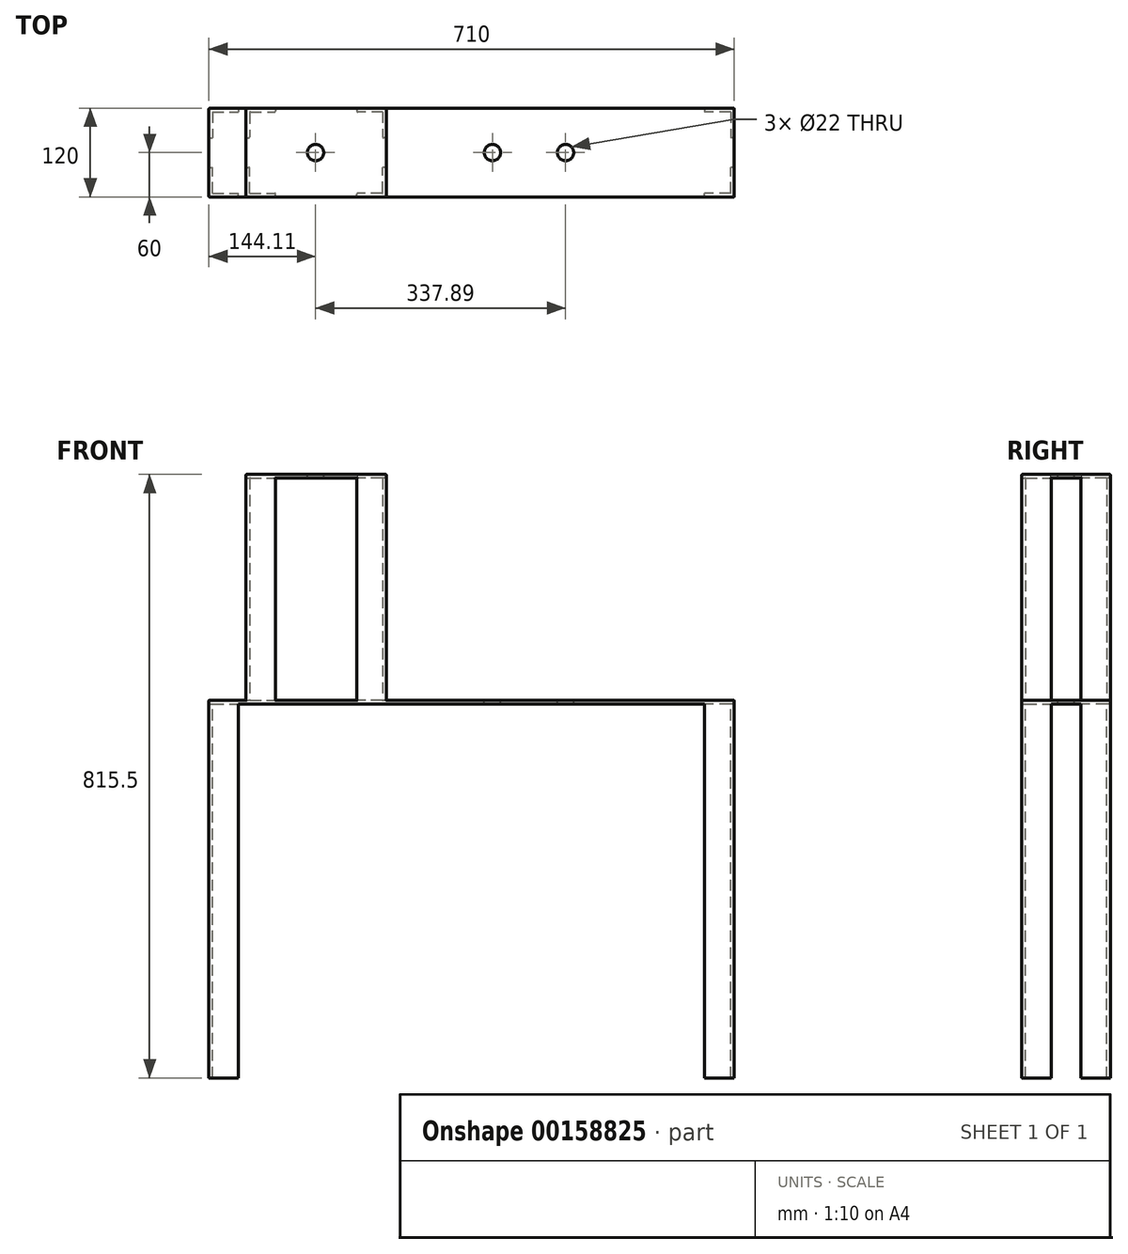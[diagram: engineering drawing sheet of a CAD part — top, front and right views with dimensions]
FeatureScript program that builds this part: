
annotation { "Feature Type Name" : "Feature", "Feature Type Description" : "" }
export const myFeature = defineFeature(function(context is Context, id is Id, definition is map)
    precondition{}
    {
        {
            var Q0;
            Q0=qCreatedBy(makeId("Top.planeOp"),FACE);
            var sketch = newSketch(context, id + "F0", { "sketchPlane" : qUnion([Q0])});
            skLineSegment(sketch, "E0.bottom", {"start": v(-355, -60) * mm, "end": v(355, -60) * mm});
            skLineSegment(sketch, "E0.top", {"start": v(-355, 60) * mm, "end": v(355, 60) * mm});
            skLineSegment(sketch, "E0.left", {"start": v(-355, -60) * mm, "end": v(-355, 60) * mm});
            skLineSegment(sketch, "E0.right", {"start": v(355, -60) * mm, "end": v(355, 60) * mm});
            skPoint(sketch, "E0.middle", {"position": v(0, 0) * mm});
            skSolve(sketch);
        }
        {
            var Q0;
            Q0=makeQuery(id+"F0.imprint","IMPRINT",FACE,{"disambiguationData":[TD([[makeQuery(id+"F0.imprint","IMPRINT",EDGE,{"derivedFrom":sQuery(id+"F0.wireOp",EDGE,"E0.bottom")}),1.0]])]});
            extrude(context, id + "F1", {"entities" : qUnion([Q0]), "depth" : 5 * mm});
        }
        {
            var Q0;
            Q0=makeQuery(id+"F1.opExtrude","CAP_FACE",FACE,{"disambiguationData":[OSD([sQuery(id+"F0.wireOp",EDGE,"E0.bottom"),sQuery(id+"F0.wireOp",EDGE,"E0.top"),sQuery(id+"F0.wireOp",EDGE,"E0.left"),sQuery(id+"F0.wireOp",EDGE,"E0.right")])],"isStart":true});
            var sketch = newSketch(context, id + "F2", { "sketchPlane" : qUnion([Q0])});
            skLineSegment(sketch, "E1", {"start": v(0, 84.03) * mm, "end": v(0, -87.79) * mm, "construction": true});
            skLineSegment(sketch, "E2", {"start": v(-372.84, 0) * mm, "end": v(344.3, 0) * mm, "construction": true});
            skSolve(sketch);
        }
        {
            var Q0;
            Q0=makeQuery(id+"F1.opExtrude","CAP_FACE",FACE,{"disambiguationData":[OSD([sQuery(id+"F0.wireOp",EDGE,"E0.bottom"),sQuery(id+"F0.wireOp",EDGE,"E0.top"),sQuery(id+"F0.wireOp",EDGE,"E0.left"),sQuery(id+"F0.wireOp",EDGE,"E0.right")])],"isStart":true});
            var sketch = newSketch(context, id + "F3", { "sketchPlane" : qUnion([Q0])});
            skLineSegment(sketch, "E3.bottom", {"start": v(-355, 60) * mm, "end": v(-350, 60) * mm});
            skLineSegment(sketch, "E3.top", {"start": v(-355, 20) * mm, "end": v(-350, 20) * mm});
            skLineSegment(sketch, "E3.left", {"start": v(-355, 60) * mm, "end": v(-355, 20) * mm});
            skLineSegment(sketch, "E3.right", {"start": v(-350, 55) * mm, "end": v(-350, 20) * mm});
            skLineSegment(sketch, "E4.bottom", {"start": v(-355, 60) * mm, "end": v(-315, 60) * mm});
            skLineSegment(sketch, "E4.top", {"start": v(-350, 55) * mm, "end": v(-315, 55) * mm});
            skLineSegment(sketch, "E4.left", {"start": v(-355, 60) * mm, "end": v(-355, 55) * mm});
            skLineSegment(sketch, "E4.right", {"start": v(-315, 60) * mm, "end": v(-315, 55) * mm});
            skLineSegment(sketch, "E5.MirrorCS", {"start": v(-350, -55) * mm, "end": v(-350, -20) * mm});
            skLineSegment(sketch, "E6.MirrorCS", {"start": v(-355, -60) * mm, "end": v(-355, -20) * mm});
            skLineSegment(sketch, "E7.MirrorCS", {"start": v(-350, -55) * mm, "end": v(-315, -55) * mm});
            skLineSegment(sketch, "E8.MirrorCS", {"start": v(-355, -60) * mm, "end": v(-315, -60) * mm});
            skLineSegment(sketch, "E9.MirrorCS", {"start": v(-315, -60) * mm, "end": v(-315, -55) * mm});
            skLineSegment(sketch, "E10.MirrorCS", {"start": v(-355, -20) * mm, "end": v(-350, -20) * mm});
            skLineSegment(sketch, "E11.MirrorCS", {"start": v(355, -20) * mm, "end": v(350, -20) * mm});
            skLineSegment(sketch, "E12.MirrorCS", {"start": v(315, -60) * mm, "end": v(315, -55) * mm});
            skLineSegment(sketch, "E13.MirrorCS", {"start": v(315, 60) * mm, "end": v(315, 55) * mm});
            skLineSegment(sketch, "E14.MirrorCS", {"start": v(355, 20) * mm, "end": v(350, 20) * mm});
            skLineSegment(sketch, "E15.MirrorCS", {"start": v(355, 60) * mm, "end": v(350, 60) * mm});
            skLineSegment(sketch, "E16.MirrorCS", {"start": v(355, 60) * mm, "end": v(355, 55) * mm});
            skLineSegment(sketch, "E17.MirrorCS", {"start": v(355, -60) * mm, "end": v(315, -60) * mm});
            skLineSegment(sketch, "E18.MirrorCS", {"start": v(350, -55) * mm, "end": v(315, -55) * mm});
            skLineSegment(sketch, "E19.MirrorCS", {"start": v(350, 55) * mm, "end": v(315, 55) * mm});
            skLineSegment(sketch, "E20.MirrorCS", {"start": v(355, 60) * mm, "end": v(315, 60) * mm});
            skLineSegment(sketch, "E21.MirrorCS", {"start": v(350, 55) * mm, "end": v(350, 20) * mm});
            skLineSegment(sketch, "E22.MirrorCS", {"start": v(355, 60) * mm, "end": v(355, 20) * mm});
            skLineSegment(sketch, "E23.MirrorCS", {"start": v(355, -60) * mm, "end": v(355, -20) * mm});
            skLineSegment(sketch, "E24.MirrorCS", {"start": v(350, -55) * mm, "end": v(350, -20) * mm});
            skSolve(sketch);
        }
        {
            var Q0;
            Q0 = qSketchRegion(id + "F3", true);
            extrude(context, id + "F4", {"entities" : qUnion([Q0]), "operationType" : NewBodyOperationType.ADD, "depth" : 505.5 * mm});
        }
        {
            var Q0;
            Q0=makeQuery(id+"F1.opExtrude","CAP_FACE",FACE,{"disambiguationData":[OSD([sQuery(id+"F0.wireOp",EDGE,"E0.bottom"),sQuery(id+"F0.wireOp",EDGE,"E0.top"),sQuery(id+"F0.wireOp",EDGE,"E0.left"),sQuery(id+"F0.wireOp",EDGE,"E0.right")])],"isStart":false});
            var sketch = newSketch(context, id + "F5", { "sketchPlane" : qUnion([Q0])});
            skLineSegment(sketch, "E25.bottom", {"start": v(-305, 60) * mm, "end": v(-300, 60) * mm});
            skLineSegment(sketch, "E25.top", {"start": v(-305, 20) * mm, "end": v(-300, 20) * mm});
            skLineSegment(sketch, "E25.left", {"start": v(-305, 60) * mm, "end": v(-305, 20) * mm});
            skLineSegment(sketch, "E25.right", {"start": v(-300, 60) * mm, "end": v(-300, 20) * mm});
            skLineSegment(sketch, "E26.bottom", {"start": v(-305, 60) * mm, "end": v(-265, 60) * mm});
            skLineSegment(sketch, "E26.top", {"start": v(-305, 55) * mm, "end": v(-265, 55) * mm});
            skLineSegment(sketch, "E26.left", {"start": v(-305, 60) * mm, "end": v(-305, 55) * mm});
            skLineSegment(sketch, "E26.right", {"start": v(-265, 60) * mm, "end": v(-265, 55) * mm});
            skLineSegment(sketch, "E27.MirrorCS", {"start": v(-305, -60) * mm, "end": v(-305, -55) * mm});
            skLineSegment(sketch, "E28.MirrorCS", {"start": v(-305, -60) * mm, "end": v(-300, -60) * mm});
            skLineSegment(sketch, "E29.MirrorCS", {"start": v(-265, -60) * mm, "end": v(-265, -55) * mm});
            skLineSegment(sketch, "E30.MirrorCS", {"start": v(-305, -20) * mm, "end": v(-300, -20) * mm});
            skLineSegment(sketch, "E31.MirrorCS", {"start": v(305, -60) * mm, "end": v(305, -55) * mm});
            skLineSegment(sketch, "E32.MirrorCS", {"start": v(-300, -60) * mm, "end": v(-300, -20) * mm});
            skLineSegment(sketch, "E33.MirrorCS", {"start": v(-305, -55) * mm, "end": v(-265, -55) * mm});
            skLineSegment(sketch, "E34.MirrorCS", {"start": v(-305, -60) * mm, "end": v(-265, -60) * mm});
            skLineSegment(sketch, "E35.MirrorCS", {"start": v(-305, -60) * mm, "end": v(-305, -20) * mm});
            skLineSegment(sketch, "E36", {"start": v(-210, 60) * mm, "end": v(-210, -80.07) * mm, "construction": true});
            skLineSegment(sketch, "E37.MirrorCS", {"start": v(-115, 60) * mm, "end": v(-120, 60) * mm});
            skLineSegment(sketch, "E38.MirrorCS", {"start": v(-155, 60) * mm, "end": v(-155, 55) * mm});
            skLineSegment(sketch, "E39.MirrorCS", {"start": v(-115, 20) * mm, "end": v(-120, 20) * mm});
            skLineSegment(sketch, "E40.MirrorCS", {"start": v(-115, -20) * mm, "end": v(-120, -20) * mm});
            skLineSegment(sketch, "E41.MirrorCS", {"start": v(-115, -60) * mm, "end": v(-120, -60) * mm});
            skLineSegment(sketch, "E42.MirrorCS", {"start": v(-115, 60) * mm, "end": v(-115, 55) * mm});
            skLineSegment(sketch, "E43.MirrorCS", {"start": v(-115, -60) * mm, "end": v(-115, -55) * mm});
            skLineSegment(sketch, "E44.MirrorCS", {"start": v(-155, -60) * mm, "end": v(-155, -55) * mm});
            skLineSegment(sketch, "E45.MirrorCS", {"start": v(-115, 60) * mm, "end": v(-155, 60) * mm});
            skLineSegment(sketch, "E46.MirrorCS", {"start": v(-120, 60) * mm, "end": v(-120, 20) * mm});
            skLineSegment(sketch, "E47.MirrorCS", {"start": v(-115, -55) * mm, "end": v(-155, -55) * mm});
            skLineSegment(sketch, "E48.MirrorCS", {"start": v(-120, -60) * mm, "end": v(-120, -20) * mm});
            skLineSegment(sketch, "E49.MirrorCS", {"start": v(-115, 55) * mm, "end": v(-155, 55) * mm});
            skLineSegment(sketch, "E50.MirrorCS", {"start": v(-115, -60) * mm, "end": v(-155, -60) * mm});
            skLineSegment(sketch, "E51.MirrorCS", {"start": v(-115, -60) * mm, "end": v(-115, -20) * mm});
            skLineSegment(sketch, "E52.MirrorCS", {"start": v(-115, 60) * mm, "end": v(-115, 20) * mm});
            skSolve(sketch);
        }
        {
            var Q0;
            Q0 = qSketchRegion(id + "F5", true);
            extrude(context, id + "F6", {"entities" : qUnion([Q0]), "operationType" : NewBodyOperationType.ADD, "depth" : 300 * mm});
        }
        {
            var Q0;
            Q0=makeQuery(id+"F6.opExtrude","CAP_FACE",FACE,{"disambiguationData":[OSD([sQuery(id+"F5.wireOp",EDGE,"E25.top"),sQuery(id+"F5.wireOp",EDGE,"E25.left"),sQuery(id+"F5.wireOp",EDGE,"E25.right"),sQuery(id+"F5.wireOp",EDGE,"E26.bottom"),sQuery(id+"F5.wireOp",EDGE,"E26.top"),sQuery(id+"F5.wireOp",EDGE,"E26.left"),sQuery(id+"F5.wireOp",EDGE,"E26.right")])],"isStart":false});
            var sketch = newSketch(context, id + "F7", { "sketchPlane" : qUnion([Q0])});
            skLineSegment(sketch, "E53.bottom", {"start": v(-305, 60) * mm, "end": v(-115, 60) * mm});
            skLineSegment(sketch, "E53.top", {"start": v(-305, -60) * mm, "end": v(-115, -60) * mm});
            skLineSegment(sketch, "E53.left", {"start": v(-305, 60) * mm, "end": v(-305, -60) * mm});
            skLineSegment(sketch, "E53.right", {"start": v(-115, 60) * mm, "end": v(-115, -60) * mm});
            skSolve(sketch);
        }
        {
            var Q0;
            Q0 = qSketchRegion(id + "F7", true);
            extrude(context, id + "F8", {"entities" : qUnion([Q0]), "operationType" : NewBodyOperationType.ADD, "depth" : 5 * mm});
        }
        {
            var Q0;
            Q0=makeQuery(id+"F8.opExtrude","CAP_EDGE",EDGE,{"disambiguationData":[OSD([sQuery(id+"F7.wireOp",EDGE,"E53.top")])],"isStart":false});
            var Q1;
            Q1=makeQuery(id+"F8.opExtrude","CAP_EDGE",EDGE,{"disambiguationData":[OSD([sQuery(id+"F7.wireOp",EDGE,"E53.right")])],"isStart":false});
            var Q2;
            Q2=makeQuery(id+"F8.boolean.opBoolean","MERGE",EDGE,{"derivedFrom":[makeQuery(id+"F6.opExtrude","SWEPT_EDGE",EDGE,{"disambiguationData":[OSD([sQuery(id+"F0.wireOp",EDGE,"E0.bottom"),sQuery(id+"F5.wireOp",EDGE,"E50.MirrorCS"),sQuery(id+"F5.wireOp",EDGE,"E51.MirrorCS")])]}),makeQuery(id+"F8.opExtrude","SWEPT_EDGE",EDGE,{"disambiguationData":[OSD([sQuery(id+"F7.wireOp",EDGE,"E53.top"),sQuery(id+"F7.wireOp",EDGE,"E53.right")])]})]});
            var Q3;
            Q3=makeQuery(id+"F6.opExtrude","SWEPT_EDGE",EDGE,{"disambiguationData":[OSD([sQuery(id+"F0.wireOp",EDGE,"E0.bottom"),sQuery(id+"F5.wireOp",EDGE,"E44.MirrorCS"),sQuery(id+"F5.wireOp",EDGE,"E50.MirrorCS")])]});
            var Q4;
            Q4=makeQuery(id+"F6.opExtrude","SWEPT_EDGE",EDGE,{"disambiguationData":[OSD([sQuery(id+"F5.wireOp",EDGE,"E40.MirrorCS"),sQuery(id+"F5.wireOp",EDGE,"E51.MirrorCS")])]});
            var Q5;
            Q5=makeQuery(id+"F8.opExtrude","CAP_EDGE",EDGE,{"disambiguationData":[OSD([sQuery(id+"F7.wireOp",EDGE,"E53.top")])],"isStart":true});
            var Q6;
            Q6=makeQuery(id+"F6.opExtrude","SWEPT_EDGE",EDGE,{"disambiguationData":[OSD([sQuery(id+"F0.wireOp",EDGE,"E0.bottom"),sQuery(id+"F5.wireOp",EDGE,"E29.MirrorCS"),sQuery(id+"F5.wireOp",EDGE,"E34.MirrorCS")])]});
            var Q7;
            Q7=makeQuery(id+"F6.opExtrude","SWEPT_EDGE",EDGE,{"disambiguationData":[OSD([sQuery(id+"F5.wireOp",EDGE,"E29.MirrorCS"),sQuery(id+"F5.wireOp",EDGE,"E33.MirrorCS")])]});
            var Q8;
            Q8=makeQuery(id+"F6.opExtrude","SWEPT_EDGE",EDGE,{"disambiguationData":[OSD([sQuery(id+"F5.wireOp",EDGE,"E25.top"),sQuery(id+"F5.wireOp",EDGE,"E25.left")])]});
            var Q9;
            Q9=makeQuery(id+"F6.opExtrude","SWEPT_EDGE",EDGE,{"disambiguationData":[OSD([sQuery(id+"F5.wireOp",EDGE,"E25.top"),sQuery(id+"F5.wireOp",EDGE,"E25.right")])]});
            var Q10;
            Q10=makeQuery(id+"F6.opExtrude","SWEPT_EDGE",EDGE,{"disambiguationData":[OSD([sQuery(id+"F5.wireOp",EDGE,"E25.right"),sQuery(id+"F5.wireOp",EDGE,"E26.top")])]});
            var Q11;
            Q11=makeQuery(id+"F6.opExtrude","SWEPT_EDGE",EDGE,{"disambiguationData":[OSD([sQuery(id+"F5.wireOp",EDGE,"E26.top"),sQuery(id+"F5.wireOp",EDGE,"E26.right")])]});
            var Q12;
            Q12=makeQuery(id+"F6.opExtrude","SWEPT_EDGE",EDGE,{"disambiguationData":[OSD([sQuery(id+"F0.wireOp",EDGE,"E0.top"),sQuery(id+"F5.wireOp",EDGE,"E26.bottom"),sQuery(id+"F5.wireOp",EDGE,"E26.right")])]});
            var Q13;
            Q13=makeQuery(id+"F6.opExtrude","SWEPT_EDGE",EDGE,{"disambiguationData":[OSD([sQuery(id+"F5.wireOp",EDGE,"E39.MirrorCS"),sQuery(id+"F5.wireOp",EDGE,"E46.MirrorCS")])]});
            var Q14;
            Q14=makeQuery(id+"F6.opExtrude","SWEPT_EDGE",EDGE,{"disambiguationData":[OSD([sQuery(id+"F5.wireOp",EDGE,"E39.MirrorCS"),sQuery(id+"F5.wireOp",EDGE,"E52.MirrorCS")])]});
            var Q15;
            Q15=makeQuery(id+"F8.opExtrude","CAP_EDGE",EDGE,{"disambiguationData":[OSD([sQuery(id+"F7.wireOp",EDGE,"E53.right")])],"isStart":true});
            var Q16;
            Q16=makeQuery(id+"F8.boolean.opBoolean","MERGE",EDGE,{"derivedFrom":[makeQuery(id+"F6.opExtrude","SWEPT_EDGE",EDGE,{"disambiguationData":[OSD([sQuery(id+"F0.wireOp",EDGE,"E0.top"),sQuery(id+"F5.wireOp",EDGE,"E45.MirrorCS"),sQuery(id+"F5.wireOp",EDGE,"E52.MirrorCS")])]}),makeQuery(id+"F8.opExtrude","SWEPT_EDGE",EDGE,{"disambiguationData":[OSD([sQuery(id+"F7.wireOp",EDGE,"E53.bottom"),sQuery(id+"F7.wireOp",EDGE,"E53.right")])]})]});
            var Q17;
            Q17=makeQuery(id+"F6.opExtrude","SWEPT_EDGE",EDGE,{"disambiguationData":[OSD([sQuery(id+"F5.wireOp",EDGE,"E38.MirrorCS"),sQuery(id+"F5.wireOp",EDGE,"E49.MirrorCS")])]});
            var Q18;
            Q18=makeQuery(id+"F8.boolean.opBoolean","MERGE",EDGE,{"derivedFrom":[makeQuery(id+"F6.opExtrude","SWEPT_EDGE",EDGE,{"disambiguationData":[OSD([sQuery(id+"F0.wireOp",EDGE,"E0.bottom"),sQuery(id+"F5.wireOp",EDGE,"E34.MirrorCS"),sQuery(id+"F5.wireOp",EDGE,"E35.MirrorCS")])]}),makeQuery(id+"F8.opExtrude","SWEPT_EDGE",EDGE,{"disambiguationData":[OSD([sQuery(id+"F7.wireOp",EDGE,"E53.top"),sQuery(id+"F7.wireOp",EDGE,"E53.left")])]})]});
            var Q19;
            Q19=makeQuery(id+"F8.opExtrude","CAP_EDGE",EDGE,{"disambiguationData":[OSD([sQuery(id+"F7.wireOp",EDGE,"E53.bottom")])],"isStart":false});
            var Q20;
            Q20=makeQuery(id+"F8.opExtrude","CAP_EDGE",EDGE,{"disambiguationData":[OSD([sQuery(id+"F7.wireOp",EDGE,"E53.bottom")])],"isStart":true});
            var Q21;
            Q21=makeQuery(id+"F6.opExtrude","SWEPT_EDGE",EDGE,{"disambiguationData":[OSD([sQuery(id+"F5.wireOp",EDGE,"E47.MirrorCS"),sQuery(id+"F5.wireOp",EDGE,"E48.MirrorCS")])]});
            var Q22;
            Q22=makeQuery(id+"F6.opExtrude","SWEPT_EDGE",EDGE,{"disambiguationData":[OSD([sQuery(id+"F5.wireOp",EDGE,"E44.MirrorCS"),sQuery(id+"F5.wireOp",EDGE,"E47.MirrorCS")])]});
            var Q23;
            Q23=makeQuery(id+"F6.opExtrude","SWEPT_EDGE",EDGE,{"disambiguationData":[OSD([sQuery(id+"F5.wireOp",EDGE,"E30.MirrorCS"),sQuery(id+"F5.wireOp",EDGE,"E35.MirrorCS")])]});
            var Q24;
            Q24=makeQuery(id+"F6.opExtrude","SWEPT_EDGE",EDGE,{"disambiguationData":[OSD([sQuery(id+"F5.wireOp",EDGE,"E30.MirrorCS"),sQuery(id+"F5.wireOp",EDGE,"E32.MirrorCS")])]});
            var Q25;
            Q25=makeQuery(id+"F8.boolean.opBoolean","MERGE",EDGE,{"derivedFrom":[makeQuery(id+"F6.opExtrude","SWEPT_EDGE",EDGE,{"disambiguationData":[OSD([sQuery(id+"F0.wireOp",EDGE,"E0.top"),sQuery(id+"F5.wireOp",EDGE,"E26.bottom"),sQuery(id+"F5.wireOp",EDGE,"E26.left")])]}),makeQuery(id+"F8.opExtrude","SWEPT_EDGE",EDGE,{"disambiguationData":[OSD([sQuery(id+"F7.wireOp",EDGE,"E53.bottom"),sQuery(id+"F7.wireOp",EDGE,"E53.left")])]})]});
            fillet(context, id + "F9", {"entities" : qUnion([Q0, Q1, Q2, Q3, Q4, Q5, Q6, Q7, Q8, Q9, Q10, Q11, Q12, Q13, Q14, Q15, Q16, Q17, Q18, Q19, Q20, Q21, Q22, Q23, Q24, Q25]), "radius" : 1 * mm, "tangentPropagation" : true, "allowEdgeOverflow" : false});
        }
        {
            var Q0;
            Q0=makeQuery(id+"F8.opExtrude","CAP_EDGE",EDGE,{"disambiguationData":[OSD([sQuery(id+"F7.wireOp",EDGE,"E53.left")])],"isStart":false});
            var Q1;
            Q1=makeQuery(id+"F8.opExtrude","CAP_EDGE",EDGE,{"disambiguationData":[OSD([sQuery(id+"F7.wireOp",EDGE,"E53.left")])],"isStart":true});
            var Q2;
            Q2=makeQuery(id+"F6.opExtrude","SWEPT_EDGE",EDGE,{"disambiguationData":[OSD([sQuery(id+"F0.wireOp",EDGE,"E0.top"),sQuery(id+"F5.wireOp",EDGE,"E38.MirrorCS"),sQuery(id+"F5.wireOp",EDGE,"E45.MirrorCS")])]});
            var Q3;
            Q3=makeQuery(id+"F1.opExtrude","CAP_EDGE",EDGE,{"disambiguationData":[OSD([sQuery(id+"F0.wireOp",EDGE,"E0.right")])],"isStart":false});
            var Q4;
            {var subQ0=sQuery(id+"F0.wireOp",EDGE,"E0.right");var subQ1=sQuery(id+"F0.wireOp",EDGE,"E0.top");Q4=makeQuery(id+"F6.boolean.opBoolean","SPLIT",EDGE,{"disambiguationData":[TD([makeQuery(id+"F1.opExtrude","SWEPT_FACE",FACE,{"disambiguationData":[OSD([subQ0])]})])],"derivedFrom":makeQuery(id+"F1.opExtrude","CAP_EDGE",EDGE,{"disambiguationData":[OSD([subQ1])],"isStart":false})});}
            var Q5;
            {var subQ0=sQuery(id+"F0.wireOp",EDGE,"E0.right");var subQ1=sQuery(id+"F0.wireOp",EDGE,"E0.bottom");Q5=makeQuery(id+"F6.boolean.opBoolean","SPLIT",EDGE,{"disambiguationData":[TD([makeQuery(id+"F1.opExtrude","SWEPT_FACE",FACE,{"disambiguationData":[OSD([subQ0])]})])],"derivedFrom":makeQuery(id+"F1.opExtrude","CAP_EDGE",EDGE,{"disambiguationData":[OSD([subQ1])],"isStart":false})});}
            var Q6;
            {var subQ0=sQuery(id+"F0.wireOp",EDGE,"E0.top");Q6=makeQuery(id+"F6.boolean.opBoolean","SPLIT",EDGE,{"disambiguationData":[TD([makeQuery(id+"F6.opExtrude","SWEPT_FACE",FACE,{"disambiguationData":[OSD([sQuery(id+"F5.wireOp",EDGE,"E26.right")])]})])],"derivedFrom":makeQuery(id+"F1.opExtrude","CAP_EDGE",EDGE,{"disambiguationData":[OSD([subQ0])],"isStart":false})});}
            var Q7;
            {var subQ0=sQuery(id+"F0.wireOp",EDGE,"E0.left");var subQ1=sQuery(id+"F0.wireOp",EDGE,"E0.top");Q7=makeQuery(id+"F6.boolean.opBoolean","SPLIT",EDGE,{"disambiguationData":[TD([makeQuery(id+"F1.opExtrude","SWEPT_FACE",FACE,{"disambiguationData":[OSD([subQ0])]})])],"derivedFrom":makeQuery(id+"F1.opExtrude","CAP_EDGE",EDGE,{"disambiguationData":[OSD([subQ1])],"isStart":false})});}
            var Q8;
            Q8=makeQuery(id+"F1.opExtrude","CAP_EDGE",EDGE,{"disambiguationData":[OSD([sQuery(id+"F0.wireOp",EDGE,"E0.left")])],"isStart":false});
            var Q9;
            Q9=makeQuery(id+"F4.boolean.opBoolean","MERGE",EDGE,{"derivedFrom":[makeQuery(id+"F1.opExtrude","SWEPT_EDGE",EDGE,{"disambiguationData":[OSD([sQuery(id+"F0.wireOp",EDGE,"E0.top"),sQuery(id+"F0.wireOp",EDGE,"E0.left")])]}),makeQuery(id+"F4.opExtrude","SWEPT_EDGE",EDGE,{"disambiguationData":[OSD([sQuery(id+"F3.wireOp",EDGE,"E6.MirrorCS"),sQuery(id+"F3.wireOp",EDGE,"E8.MirrorCS")])]})]});
            var Q10;
            Q10=makeQuery(id+"F4.boolean.opBoolean","MERGE",EDGE,{"derivedFrom":[makeQuery(id+"F1.opExtrude","SWEPT_EDGE",EDGE,{"disambiguationData":[OSD([sQuery(id+"F0.wireOp",EDGE,"E0.top"),sQuery(id+"F0.wireOp",EDGE,"E0.right")])]}),makeQuery(id+"F4.opExtrude","SWEPT_EDGE",EDGE,{"disambiguationData":[OSD([sQuery(id+"F3.wireOp",EDGE,"E17.MirrorCS"),sQuery(id+"F3.wireOp",EDGE,"E23.MirrorCS")])]})]});
            var Q11;
            Q11=makeQuery(id+"F4.boolean.opBoolean","MERGE",EDGE,{"derivedFrom":[makeQuery(id+"F1.opExtrude","SWEPT_EDGE",EDGE,{"disambiguationData":[OSD([sQuery(id+"F0.wireOp",EDGE,"E0.bottom"),sQuery(id+"F0.wireOp",EDGE,"E0.right")])]}),makeQuery(id+"F4.opExtrude","SWEPT_EDGE",EDGE,{"disambiguationData":[OSD([sQuery(id+"F3.wireOp",EDGE,"E20.MirrorCS"),sQuery(id+"F3.wireOp",EDGE,"E22.MirrorCS")])]})]});
            var Q12;
            Q12=makeQuery(id+"F4.boolean.opBoolean","MERGE",EDGE,{"derivedFrom":[makeQuery(id+"F1.opExtrude","SWEPT_EDGE",EDGE,{"disambiguationData":[OSD([sQuery(id+"F0.wireOp",EDGE,"E0.bottom"),sQuery(id+"F0.wireOp",EDGE,"E0.left")])]}),makeQuery(id+"F4.opExtrude","SWEPT_EDGE",EDGE,{"disambiguationData":[OSD([sQuery(id+"F3.wireOp",EDGE,"E4.bottom"),sQuery(id+"F3.wireOp",EDGE,"E4.left")])]})]});
            fillet(context, id + "F10", {"entities" : qUnion([Q0, Q1, Q2, Q3, Q4, Q5, Q6, Q7, Q8, Q9, Q10, Q11, Q12]), "radius" : 1 * mm, "tangentPropagation" : true, "allowEdgeOverflow" : false});
        }
        {
            var Q0;
            Q0=makeQuery(id+"F1.opExtrude","CAP_FACE",FACE,{"disambiguationData":[OSD([sQuery(id+"F0.wireOp",EDGE,"E0.bottom"),sQuery(id+"F0.wireOp",EDGE,"E0.top"),sQuery(id+"F0.wireOp",EDGE,"E0.left"),sQuery(id+"F0.wireOp",EDGE,"E0.right")])],"isStart":false});
            var sketch = newSketch(context, id + "F11", { "sketchPlane" : qUnion([Q0])});
            skCircle(sketch, "E54", {"center": v(127, 0) * mm, "radius": 11 * mm});
            skCircle(sketch, "E55", {"center": v(28.15, 0) * mm, "radius": 11 * mm});
            skSolve(sketch);
        }
        {
            var Q0;
            Q0 = qSketchRegion(id + "F11", true);
            extrude(context, id + "F12", {"entities" : qUnion([Q0]), "operationType" : NewBodyOperationType.REMOVE, "oppositeDirection" : true, "depth" : 25 * mm});
        }
        {
            var Q0;
            Q0=makeQuery(id+"F8.opExtrude","CAP_FACE",FACE,{"disambiguationData":[OSD([sQuery(id+"F7.wireOp",EDGE,"E53.bottom"),sQuery(id+"F7.wireOp",EDGE,"E53.top"),sQuery(id+"F7.wireOp",EDGE,"E53.left"),sQuery(id+"F7.wireOp",EDGE,"E53.right")])],"isStart":false});
            var sketch = newSketch(context, id + "F13", { "sketchPlane" : qUnion([Q0])});
            skCircle(sketch, "E56", {"center": v(-210.89, 0) * mm, "radius": 11 * mm});
            skSolve(sketch);
        }
        {
            var Q0;
            Q0 = qSketchRegion(id + "F13", true);
            extrude(context, id + "F14", {"entities" : qUnion([Q0]), "operationType" : NewBodyOperationType.REMOVE, "oppositeDirection" : true, "depth" : 25 * mm});
        }
    });
